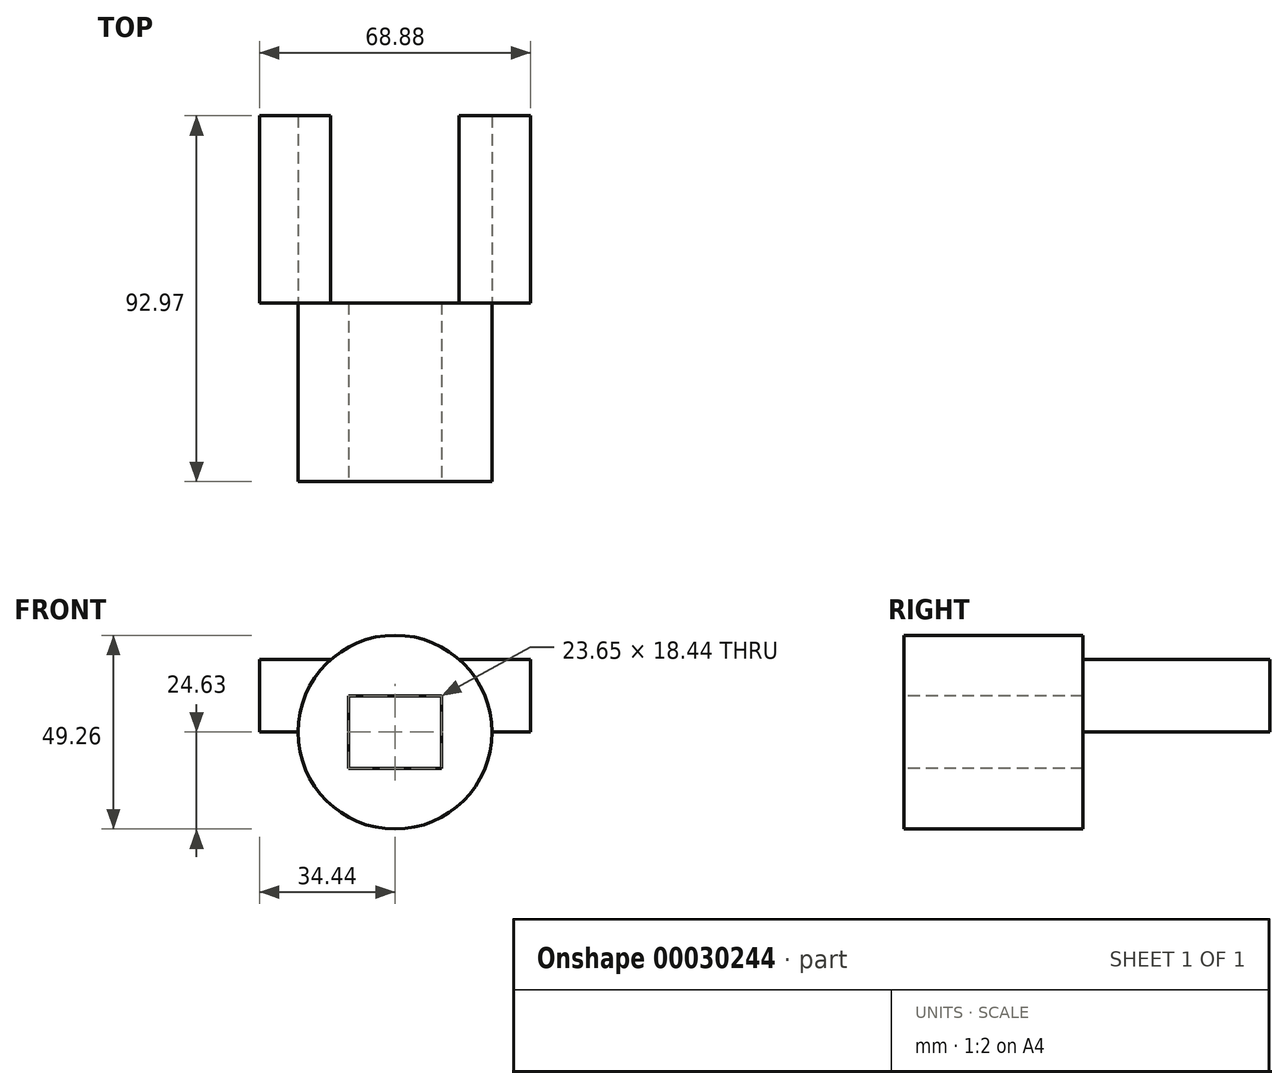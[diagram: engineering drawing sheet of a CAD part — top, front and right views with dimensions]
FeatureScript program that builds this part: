
annotation { "Feature Type Name" : "Feature", "Feature Type Description" : "" }
export const myFeature = defineFeature(function(context is Context, id is Id, definition is map)
    precondition{}
    {
        {
            var Q0;
            Q0=qCreatedBy(makeId("Front.planeOp"),FACE);
            var sketch = newSketch(context, id + "F0", { "sketchPlane" : qUnion([Q0])});
            skCircle(sketch, "E0", {"center": v(0, 0) * mm, "radius": 24.63 * mm});
            skLineSegment(sketch, "E1.rect.bottom", {"start": v(11.82, -9.22) * mm, "end": v(-11.82, -9.22) * mm});
            skLineSegment(sketch, "E1.rect.top", {"start": v(11.82, 9.22) * mm, "end": v(-11.82, 9.22) * mm});
            skLineSegment(sketch, "E1.rect.left", {"start": v(11.82, -9.22) * mm, "end": v(11.82, 9.22) * mm});
            skLineSegment(sketch, "E1.rect.right", {"start": v(-11.82, -9.22) * mm, "end": v(-11.82, 9.22) * mm});
            skSolve(sketch);
        }
        {
            var Q0;
            Q0=qCreatedBy(makeId("Right.planeOp"),FACE);
            var sketch = newSketch(context, id + "F1", { "sketchPlane" : qUnion([Q0])});
            skPoint(sketch, "E2", {"position": v(-49.34, 0) * mm});
            skSolve(sketch);
        }
        {
            var Q0;
            Q0=makeQuery(id+"F0.imprint","IMPRINT",FACE,{"disambiguationData":[TD([[makeQuery(id+"F0.imprint","IMPRINT",EDGE,{"derivedFrom":sQuery(id+"F0.wireOp",EDGE,"E0")}),1.0]])]});
            extrude(context, id + "F2", {"entities" : qUnion([Q0]), "oppositeDirection" : true, "depth" : 45.46 * mm});
        }
        {
            var Q0;
            Q0=makeQuery(id+"F2.opExtrude","CAP_FACE",FACE,{"disambiguationData":[OSD([sQuery(id+"F0.wireOp",EDGE,"E0"),sQuery(id+"F0.wireOp",EDGE,"E1.rect.bottom"),sQuery(id+"F0.wireOp",EDGE,"E1.rect.top"),sQuery(id+"F0.wireOp",EDGE,"E1.rect.left"),sQuery(id+"F0.wireOp",EDGE,"E1.rect.right")])],"isStart":false});
            var sketch = newSketch(context, id + "F3", { "sketchPlane" : qUnion([Q0])});
            skLineSegment(sketch, "E3.rect.bottom", {"start": v(34.44, 0) * mm, "end": v(-34.44, 0) * mm});
            skLineSegment(sketch, "E3.rect.top", {"start": v(34.44, 18.44) * mm, "end": v(-34.44, 18.44) * mm});
            skLineSegment(sketch, "E3.rect.left", {"start": v(34.44, 0) * mm, "end": v(34.44, 18.44) * mm});
            skLineSegment(sketch, "E3.rect.right", {"start": v(-34.44, 0) * mm, "end": v(-34.44, 18.44) * mm});
            skPoint(sketch, "E3.rect.middle", {"position": v(0, 9.22) * mm});
            skSolve(sketch);
        }
        {
            var Q0;
            {var subQ5=sQuery(id+"F3.wireOp",EDGE,"E3.rect.left");Q0=makeQuery(id+"F3.imprint","IMPRINT",FACE,{"disambiguationData":[TD([[makeQuery(id+"F3.imprint","IMPRINT",EDGE,{"derivedFrom":subQ5}),1.0]])]});}
            var Q1;
            {var subQ5=sQuery(id+"F3.wireOp",EDGE,"E3.rect.right");Q1=makeQuery(id+"F3.imprint","IMPRINT",FACE,{"disambiguationData":[TD([[makeQuery(id+"F3.imprint","IMPRINT",EDGE,{"derivedFrom":subQ5}),-1.0]])]});}
            extrude(context, id + "F4", {"entities" : qUnion([Q0, Q1]), "depth" : 47.52 * mm});
        }
    });
